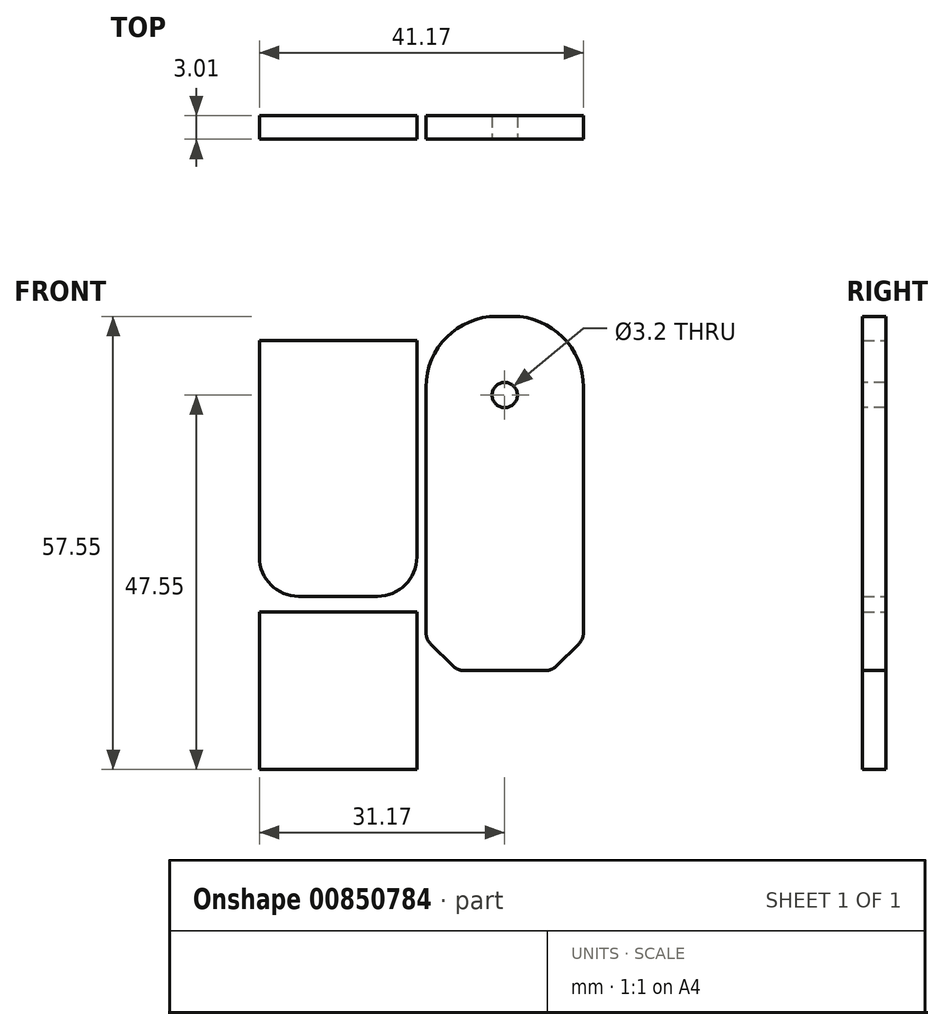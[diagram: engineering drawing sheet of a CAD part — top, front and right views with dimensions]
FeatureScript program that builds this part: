
annotation { "Feature Type Name" : "Feature", "Feature Type Description" : "" }
export const myFeature = defineFeature(function(context is Context, id is Id, definition is map)
    precondition{}
    {
        {
            var Q0;
            Q0=qCreatedBy(makeId("Top.planeOp"),FACE);
            var sketch = newSketch(context, id + "F0", { "sketchPlane" : qUnion([Q0])});
            skLineSegment(sketch, "E0.bottom", {"start": v(10, 22.5) * mm, "end": v(-10, 22.5) * mm});
            skLineSegment(sketch, "E0.top", {"start": v(10, -22.5) * mm, "end": v(-10, -22.5) * mm});
            skLineSegment(sketch, "E0.left", {"start": v(10, 22.5) * mm, "end": v(10, -22.5) * mm});
            skLineSegment(sketch, "E0.right", {"start": v(-10, 22.5) * mm, "end": v(-10, -22.5) * mm});
            skPoint(sketch, "E0.middle", {"position": v(0, 0) * mm});
            skCircle(sketch, "E1", {"center": v(0, -12.5) * mm, "radius": 1.6 * mm});
            skCircle(sketch, "E2", {"center": v(0, -12.5) * mm, "radius": 10 * mm, "construction": true});
            skSolve(sketch);
        }
        {
            var Q0;
            Q0=qSketchRegion(id+"F0",true);
            extrude(context, id + "F1", {"entities" : qUnion([Q0]), "depth" : 3 * mm});
        }
        {
            var Q0;
            Q0=makeQuery(id+"F1.opExtrude","SWEPT_EDGE",EDGE,{"disambiguationData":[OSD([sQuery(id+"F0.wireOp",EDGE,"E0.top"),sQuery(id+"F0.wireOp",EDGE,"E0.left")])]});
            var Q1;
            Q1=makeQuery(id+"F1.opExtrude","SWEPT_EDGE",EDGE,{"disambiguationData":[OSD([sQuery(id+"F0.wireOp",EDGE,"E0.top"),sQuery(id+"F0.wireOp",EDGE,"E0.right")])]});
            fillet(context, id + "F2", {"entities" : qUnion([Q0, Q1]), "radius" : 9 * mm, "tangentPropagation" : true, "allowEdgeOverflow" : false});
        }
        {
            var Q0;
            Q0=makeQuery(id+"F1.opExtrude","SWEPT_EDGE",EDGE,{"disambiguationData":[OSD([sQuery(id+"F0.wireOp",EDGE,"E0.bottom"),sQuery(id+"F0.wireOp",EDGE,"E0.right")])]});
            var Q1;
            Q1=makeQuery(id+"F1.opExtrude","SWEPT_EDGE",EDGE,{"disambiguationData":[OSD([sQuery(id+"F0.wireOp",EDGE,"E0.bottom"),sQuery(id+"F0.wireOp",EDGE,"E0.left")])]});
            chamfer(context, id + "F3", {"entities" : qUnion([Q0, Q1]), "width" : 4 * mm, "tangentPropagation" : true});
        }
        {
            var Q0;
            {var subQ0=sQuery(id+"F0.wireOp",EDGE,"E0.bottom");Q0=makeQuery(id+"F3.opChamfer","BLEND_EDGE",EDGE,{"blendedFrom":[makeQuery(id+"F1.opExtrude","SWEPT_EDGE",EDGE,{"disambiguationData":[OSD([subQ0,sQuery(id+"F0.wireOp",EDGE,"E0.right")])]}),makeQuery(id+"F1.opExtrude","SWEPT_FACE",FACE,{"disambiguationData":[OSD([subQ0])]})],"blendedInto":[makeQuery(id+"F1.opExtrude","SWEPT_FACE",FACE,{"disambiguationData":[OSD([subQ0])]})]});}
            var Q1;
            {var subQ0=sQuery(id+"F0.wireOp",EDGE,"E0.bottom");Q1=makeQuery(id+"F3.opChamfer","BLEND_EDGE",EDGE,{"blendedFrom":[makeQuery(id+"F1.opExtrude","SWEPT_EDGE",EDGE,{"disambiguationData":[OSD([subQ0,sQuery(id+"F0.wireOp",EDGE,"E0.left")])]}),makeQuery(id+"F1.opExtrude","SWEPT_FACE",FACE,{"disambiguationData":[OSD([subQ0])]})],"blendedInto":[makeQuery(id+"F1.opExtrude","SWEPT_FACE",FACE,{"disambiguationData":[OSD([subQ0])]})]});}
            var Q2;
            {var subQ0=sQuery(id+"F0.wireOp",EDGE,"E0.left");Q2=makeQuery(id+"F3.opChamfer","BLEND_EDGE",EDGE,{"blendedFrom":[makeQuery(id+"F1.opExtrude","SWEPT_EDGE",EDGE,{"disambiguationData":[OSD([sQuery(id+"F0.wireOp",EDGE,"E0.bottom"),subQ0])]}),makeQuery(id+"F1.opExtrude","SWEPT_FACE",FACE,{"disambiguationData":[OSD([subQ0])]})],"blendedInto":[makeQuery(id+"F1.opExtrude","SWEPT_FACE",FACE,{"disambiguationData":[OSD([subQ0])]})]});}
            var Q3;
            {var subQ0=sQuery(id+"F0.wireOp",EDGE,"E0.right");Q3=makeQuery(id+"F3.opChamfer","BLEND_EDGE",EDGE,{"blendedFrom":[makeQuery(id+"F1.opExtrude","SWEPT_EDGE",EDGE,{"disambiguationData":[OSD([sQuery(id+"F0.wireOp",EDGE,"E0.bottom"),subQ0])]}),makeQuery(id+"F1.opExtrude","SWEPT_FACE",FACE,{"disambiguationData":[OSD([subQ0])]})],"blendedInto":[makeQuery(id+"F1.opExtrude","SWEPT_FACE",FACE,{"disambiguationData":[OSD([subQ0])]})]});}
            fillet(context, id + "F4", {"entities" : qUnion([Q0, Q1, Q2, Q3]), "radius" : 2 * mm, "tangentPropagation" : true, "allowEdgeOverflow" : false});
        }
        {
            var Q0;
            Q0=qCreatedBy(makeId("Front.planeOp"),FACE);
            var sketch = newSketch(context, id + "F5", { "sketchPlane" : qUnion([Q0])});
            skLineSegment(sketch, "E3.bottom", {"start": v(-32.77, -42.25) * mm, "end": v(-52.77, -42.25) * mm});
            skLineSegment(sketch, "E3.top", {"start": v(-32.77, -22.25) * mm, "end": v(-52.77, -22.25) * mm});
            skLineSegment(sketch, "E3.left", {"start": v(-32.77, -42.25) * mm, "end": v(-32.77, -22.25) * mm});
            skLineSegment(sketch, "E3.right", {"start": v(-52.77, -42.25) * mm, "end": v(-52.77, -22.25) * mm});
            skPoint(sketch, "E3.middle", {"position": v(-42.77, -32.25) * mm});
            skLineSegment(sketch, "E4.bottom", {"start": v(-52.77, -10.37) * mm, "end": v(-32.77, -10.37) * mm});
            skLineSegment(sketch, "E4.top", {"start": v(-52.77, 22.1) * mm, "end": v(-32.77, 22.1) * mm});
            skLineSegment(sketch, "E4.left", {"start": v(-52.77, -10.37) * mm, "end": v(-52.77, 22.1) * mm});
            skLineSegment(sketch, "E4.right", {"start": v(-32.77, -10.37) * mm, "end": v(-32.77, 22.1) * mm});
            skSolve(sketch);
        }
        {
            var Q0;
            Q0=qSketchRegion(id+"F5",true);
            extrude(context, id + "F6", {"entities" : qUnion([Q0]), "depth" : 3 * mm});
        }
        {
            var Q0;
            Q0=makeQuery(id+"F6.opExtrude","SWEPT_EDGE",EDGE,{"disambiguationData":[OSD([sQuery(id+"F5.wireOp",EDGE,"E4.bottom"),sQuery(id+"F5.wireOp",EDGE,"E4.right")])]});
            var Q1;
            Q1=makeQuery(id+"F6.opExtrude","SWEPT_EDGE",EDGE,{"disambiguationData":[OSD([sQuery(id+"F5.wireOp",EDGE,"E4.bottom"),sQuery(id+"F5.wireOp",EDGE,"E4.left")])]});
            fillet(context, id + "F7", {"entities" : qUnion([Q0, Q1]), "radius" : 5 * mm, "tangentPropagation" : true, "allowEdgeOverflow" : false});
        }
        {
            var Q0;
            Q0=makeQuery(id+"F1.opExtrude","CAP_EDGE",EDGE,{"disambiguationData":[OSD([sQuery(id+"F0.wireOp",EDGE,"E0.bottom")])],"isStart":false});
            cPoint(context, id + "F8", {"entities" : qUnion([Q0]), "parameter" : 0.5});
        }
        {
            var Q0;
            Q0=makeQuery(id+"F1.opExtrude","SWEPT_BODY",BODY,{"disambiguationData":[OSD([sQuery(id+"F0.wireOp",EDGE,"E0.bottom"),sQuery(id+"F0.wireOp",EDGE,"E0.top"),sQuery(id+"F0.wireOp",EDGE,"E0.left"),sQuery(id+"F0.wireOp",EDGE,"E0.right"),sQuery(id+"F0.wireOp",EDGE,"E1")])]});
            var Q1;
            Q1=qCreatedBy(id+"F8",VERTEX);
            var Q2;
            Q2=makeQuery(id+"F1.opExtrude","CAP_EDGE",EDGE,{"disambiguationData":[OSD([sQuery(id+"F0.wireOp",EDGE,"E0.bottom")])],"isStart":false});
            var Q3;
            Q3=makeQuery(id+"F1.opExtrude","CAP_EDGE",EDGE,{"disambiguationData":[OSD([sQuery(id+"F0.wireOp",EDGE,"E0.bottom")])],"isStart":false});
            transform(context, id + "F9", {"entities" : qUnion([Q0]), "transformType" : TransformType.ROTATION, "transformAxis" : qUnion([Q3]), "angle" : 90 * degree, "makeCopy" : false});
        }
        {
            var Q0;
            Q0=makeQuery(id+"F1.opExtrude","SWEPT_BODY",BODY,{"disambiguationData":[OSD([sQuery(id+"F0.wireOp",EDGE,"E0.bottom"),sQuery(id+"F0.wireOp",EDGE,"E0.top"),sQuery(id+"F0.wireOp",EDGE,"E0.left"),sQuery(id+"F0.wireOp",EDGE,"E0.right"),sQuery(id+"F0.wireOp",EDGE,"E1")])]});
            transform(context, id + "F10", {"entities" : qUnion([Q0]), "transformType" : TransformType.TRANSLATION_3D, "dx" : -21.6 * mm, "dy" : -22.51 * mm, "dz" : 0 * mm, "makeCopy" : false});
        }
        {
            var Q0;
            Q0=makeQuery(id+"F6.opExtrude","SWEPT_BODY",BODY,{"disambiguationData":[OSD([sQuery(id+"F5.wireOp",EDGE,"E4.bottom"),sQuery(id+"F5.wireOp",EDGE,"E4.top"),sQuery(id+"F5.wireOp",EDGE,"E4.left"),sQuery(id+"F5.wireOp",EDGE,"E4.right")])]});
            transform(context, id + "F11", {"entities" : qUnion([Q0]), "transformType" : TransformType.TRANSLATION_3D, "dx" : 0 * mm, "dy" : 0 * mm, "dz" : 22.8 * mm, "makeCopy" : false});
        }
        {
            var Q0;
            Q0=makeQuery(id+"F6.opExtrude","SWEPT_BODY",BODY,{"disambiguationData":[OSD([sQuery(id+"F5.wireOp",EDGE,"E3.bottom"),sQuery(id+"F5.wireOp",EDGE,"E3.top"),sQuery(id+"F5.wireOp",EDGE,"E3.left"),sQuery(id+"F5.wireOp",EDGE,"E3.right")])]});
            transform(context, id + "F12", {"entities" : qUnion([Q0]), "transformType" : TransformType.TRANSLATION_3D, "dx" : 0 * mm, "dy" : 0 * mm, "dz" : 32.7 * mm, "makeCopy" : false});
        }
    });
